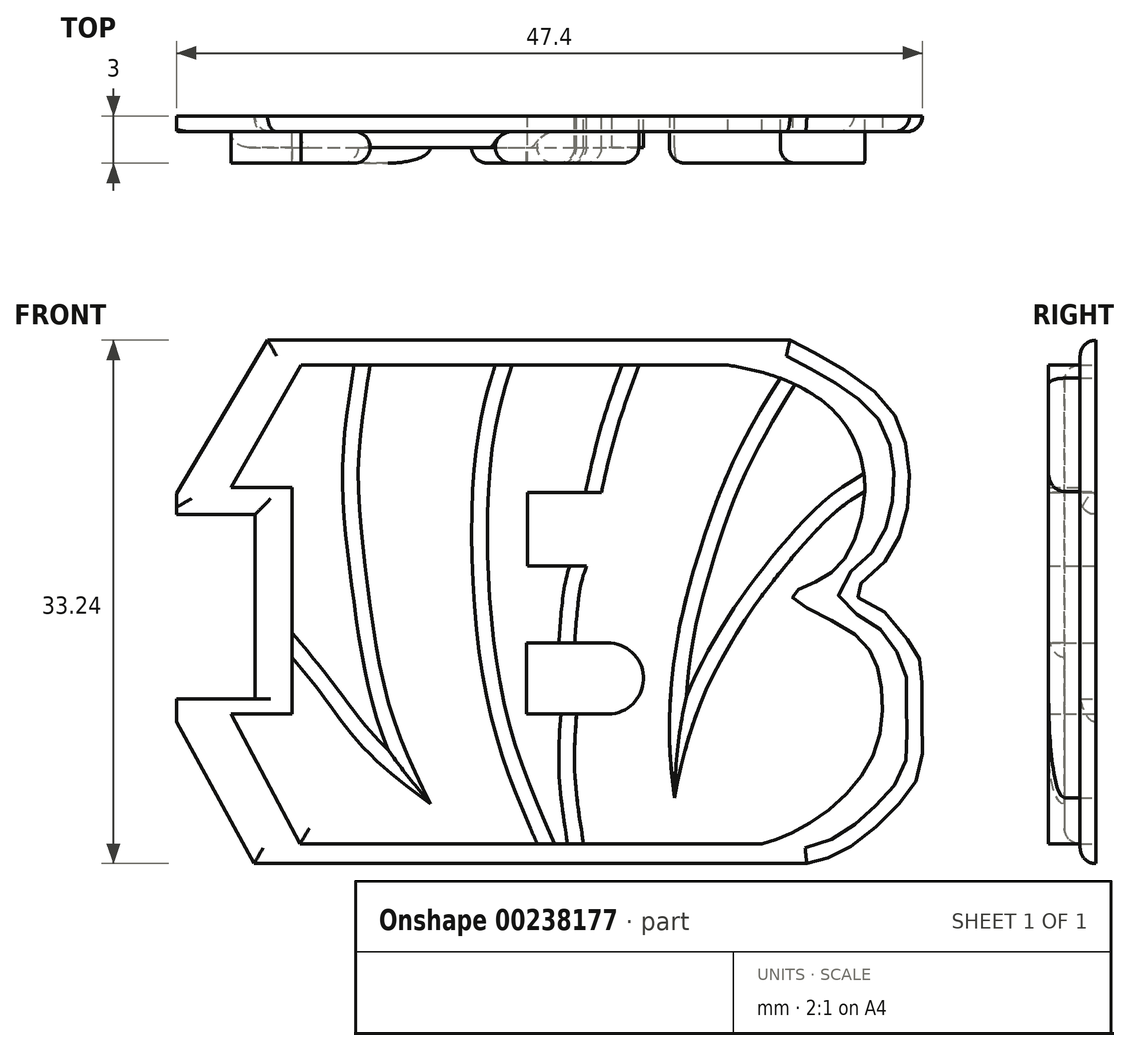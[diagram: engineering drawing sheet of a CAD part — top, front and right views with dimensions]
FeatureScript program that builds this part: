
annotation { "Feature Type Name" : "Feature", "Feature Type Description" : "" }
export const myFeature = defineFeature(function(context is Context, id is Id, definition is map)
    precondition{}
    {
        {
            var Q0;
            Q0=qCreatedBy(makeId("Front.planeOp"),FACE);
            var sketch = newSketch(context, id + "F0", { "sketchPlane" : qUnion([Q0])});
            skLineSegment(sketch, "E0", {"start": v(14.04, 53.13) * mm, "end": v(19.84, 62.86) * mm});
            skLineSegment(sketch, "E1", {"start": v(19.84, 62.86) * mm, "end": v(53.01, 62.86) * mm});
            skFitSpline(sketch, "E2", {"points": [v(53.01, 62.86) * mm, v(55.4, 61.6) * mm, v(58.74, 59.26) * mm, v(60.2, 56.87) * mm, v(60.6, 53.6) * mm, v(60.07, 50.67) * mm, v(58.67, 48.4) * mm, v(57.07, 46.8) * mm, v(58.67, 45.87) * mm, v(60.94, 43.14) * mm, v(61.34, 42.28) * mm, v(61.4, 38.95) * mm, v(61.27, 35.55) * mm, v(60, 33.48) * mm, v(57.6, 31.22) * mm, v(55.54, 30.02) * mm, v(54.08, 29.62) * mm], "startDerivative": vector(35.52, -17.88) * mm, "endDerivative": vector(-30.19, -6.38) * mm});
            skLineSegment(sketch, "E3", {"start": v(54.08, 29.62) * mm, "end": v(18.97, 29.62) * mm});
            skLineSegment(sketch, "E4", {"start": v(18.97, 29.62) * mm, "end": v(14.04, 38.61) * mm});
            skLineSegment(sketch, "E5", {"start": v(14.04, 38.61) * mm, "end": v(14.04, 40.08) * mm});
            skLineSegment(sketch, "E6", {"start": v(14.04, 40.08) * mm, "end": v(18.5, 40.08) * mm});
            skLineSegment(sketch, "E7", {"start": v(19.04, 40.74) * mm, "end": v(19.04, 51.8) * mm});
            skLineSegment(sketch, "E8", {"start": v(19.04, 51.8) * mm, "end": v(14.04, 51.8) * mm});
            skLineSegment(sketch, "E9", {"start": v(14.04, 51.8) * mm, "end": v(14.04, 53.13) * mm});
            skLineSegment(sketch, "E10", {"start": v(19.04, 40.74) * mm, "end": v(19.04, 40.07) * mm});
            skLineSegment(sketch, "E11", {"start": v(19.04, 40.07) * mm, "end": v(18.5, 40.08) * mm});
            skLineSegment(sketch, "E12", {"start": v(17.51, 53.52) * mm, "end": v(21.96, 61.29) * mm});
            skLineSegment(sketch, "E13", {"start": v(21.96, 61.29) * mm, "end": v(49.06, 61.29) * mm});
            skLineSegment(sketch, "E14", {"start": v(17.51, 53.52) * mm, "end": v(21.4, 53.52) * mm});
            skLineSegment(sketch, "E15", {"start": v(21.4, 53.52) * mm, "end": v(21.4, 39.13) * mm});
            skLineSegment(sketch, "E16", {"start": v(21.4, 39.13) * mm, "end": v(17.51, 39.13) * mm});
            skLineSegment(sketch, "E17", {"start": v(17.51, 39.13) * mm, "end": v(21.89, 30.87) * mm});
            skLineSegment(sketch, "E18", {"start": v(21.89, 30.87) * mm, "end": v(51.25, 30.87) * mm});
            skFitSpline(sketch, "E19", {"points": [v(51.25, 30.87) * mm, v(53.15, 31.58) * mm, v(56.47, 33.9) * mm, v(58.66, 37.57) * mm, v(58.66, 41.67) * mm, v(56.9, 44.35) * mm, v(53.15, 46.6) * mm, v(54.7, 47.53) * mm, v(56.75, 49.43) * mm, v(57.74, 54.09) * mm, v(55.77, 58.4) * mm, v(52.02, 60.58) * mm, v(49.06, 61.29) * mm], "startDerivative": vector(28.18, 8.53) * mm, "endDerivative": vector(-37.02, 6.74) * mm});
            skLineSegment(sketch, "E20", {"start": v(36.29, 39.13) * mm, "end": v(36.29, 43.64) * mm});
            skLineSegment(sketch, "E21", {"start": v(36.29, 43.64) * mm, "end": v(41.44, 43.64) * mm});
            skLineSegment(sketch, "E22", {"start": v(36.29, 39.13) * mm, "end": v(41.72, 39.13) * mm});
            skArc(sketch, "E23", {"start": v(41.44, 43.64) * mm, "mid": v(43.7, 41.52) * mm, "end": v(41.72, 39.13) * mm});
            skLineSegment(sketch, "E24", {"start": v(36.36, 48.51) * mm, "end": v(36.36, 53.2) * mm});
            skLineSegment(sketch, "E25", {"start": v(36.36, 53.2) * mm, "end": v(41.44, 53.2) * mm});
            skLineSegment(sketch, "E26", {"start": v(36.36, 48.51) * mm, "end": v(41.63, 48.51) * mm});
            skPoint(sketch, "E27.3.internal.snap0", {"position": v(38.9, 53.2) * mm});
            skFitSpline(sketch, "E28", {"points": [v(41.63, 48.51) * mm, v(42.75, 49.1) * mm, v(43.41, 50.24) * mm, v(43.32, 51.79) * mm, v(42.75, 52.72) * mm, v(41.44, 53.2) * mm], "startDerivative": vector(6.1, 2.42) * mm, "endDerivative": vector(-7.14, 1.68) * mm});
            skFitSpline(sketch, "E29", {"points": [v(34.3, 61.29) * mm, v(33.63, 58.94) * mm, v(32.92, 54.27) * mm, v(33.05, 45.07) * mm, v(34.56, 37.02) * mm, v(36.96, 30.87) * mm], "startDerivative": vector(-5.32, -17.12) * mm, "endDerivative": vector(12.35, -28.27) * mm});
            skFitSpline(sketch, "E30", {"points": [v(43.41, 61.29) * mm, v(42.03, 57.25) * mm, v(41.03, 53.2) * mm], "startDerivative": vector(-2.94, -8) * mm, "endDerivative": vector(-1.82, -8.19) * mm});
            skFitSpline(sketch, "E31", {"points": [v(40.1, 48.51) * mm, v(39.73, 47.34) * mm, v(39.34, 43.64) * mm], "startDerivative": vector(-1.1, -2.73) * mm, "endDerivative": vector(-0.49, -6.66) * mm});
            skFitSpline(sketch, "E32", {"points": [v(39.46, 39.13) * mm, v(39.34, 35.47) * mm, v(39.9, 30.87) * mm], "startDerivative": vector(-0.56, -7.56) * mm, "endDerivative": vector(1.41, -8.93) * mm});
            skFitSpline(sketch, "E33", {"points": [v(21.4, 42.7) * mm, v(23.37, 40.25) * mm, v(26.06, 36.84) * mm, v(30.18, 33.4) * mm], "startDerivative": vector(6.77, -8.11) * mm, "endDerivative": vector(11.74, -8.81) * mm});
            skFitSpline(sketch, "E34", {"points": [v(52.4, 60.45) * mm, v(51.25, 58.6) * mm, v(49.04, 54.31) * mm, v(47.3, 49.52) * mm, v(45.95, 44.37) * mm, v(45.35, 38.03) * mm, v(45.67, 33.8) * mm], "startDerivative": vector(-9.1, -14.25) * mm, "endDerivative": vector(2.9, -24.71) * mm});
            skFitSpline(sketch, "E35", {"points": [v(45.67, 33.8) * mm, v(46.12, 35.86) * mm, v(47.23, 39.55) * mm, v(49.2, 43.55) * mm, v(51.5, 47) * mm, v(55.66, 51.75) * mm, v(57.76, 53.25) * mm], "startDerivative": vector(3.17, 15.46) * mm, "endDerivative": vector(14, 8.38) * mm});
            skFitSpline(sketch, "E36", {"points": [v(30.18, 33.4) * mm, v(27.6, 39.53) * mm, v(26.18, 47.33) * mm, v(25.6, 54.63) * mm, v(26.35, 61.29) * mm], "startDerivative": vector(-11.9, 24.29) * mm, "endDerivative": vector(4.43, 27.26) * mm});
            skSolve(sketch);
        }
        {
            var Q0;
            Q0=makeQuery(id+"F0.imprint","IMPRINT",FACE,{"disambiguationData":[TD([[makeQuery(id+"F0.imprint","IMPRINT",EDGE,{"derivedFrom":sQuery(id+"F0.wireOp",EDGE,"E0")}),-1.0]])]});
            extrude(context, id + "F1", {"entities" : qUnion([Q0]), "depth" : 1 * mm});
        }
        {
            var Q0;
            {var subQ1=sQuery(id+"F0.wireOp",EDGE,"E16");Q0=makeQuery(id+"F0.imprint","IMPRINT",FACE,{"disambiguationData":[TD([[makeQuery(id+"F0.imprint","IMPRINT",EDGE,{"derivedFrom":subQ1}),1.0]])]});}
            var Q1;
            {var subQ5=sQuery(id+"F0.wireOp",EDGE,"E23");Q1=makeQuery(id+"F0.imprint","IMPRINT",FACE,{"disambiguationData":[TD([[makeQuery(id+"F0.imprint","IMPRINT",EDGE,{"derivedFrom":subQ5}),1.0]])]});}
            extrude(context, id + "F2", {"entities" : qUnion([Q0, Q1]), "operationType" : NewBodyOperationType.ADD, "depth" : 2 * mm});
        }
        {
            var Q0;
            {var subQ4=sQuery(id+"F0.wireOp",EDGE,"E12");Q0=makeQuery(id+"F0.imprint","IMPRINT",FACE,{"disambiguationData":[TD([[makeQuery(id+"F0.imprint","IMPRINT",EDGE,{"derivedFrom":subQ4}),-1.0]])]});}
            var Q1;
            {var subQ4=sQuery(id+"F0.wireOp",EDGE,"E20");Q1=makeQuery(id+"F0.imprint","IMPRINT",FACE,{"disambiguationData":[TD([[makeQuery(id+"F0.imprint","IMPRINT",EDGE,{"derivedFrom":subQ4}),1.0]])]});}
            var Q2;
            {var subQ0=sQuery(id+"F0.wireOp",EDGE,"E34");Q2=makeQuery(id+"F0.imprint","IMPRINT",FACE,{"disambiguationData":[TD([[makeQuery(id+"F0.imprint","IMPRINT",EDGE,{"derivedFrom":subQ0}),1.0]])]});}
            extrude(context, id + "F3", {"entities" : qUnion([Q0, Q1, Q2]), "operationType" : NewBodyOperationType.ADD, "depth" : 3 * mm});
        }
        {
            var Q0;
            Q0=makeQuery(id+"F3.opExtrude","CAP_EDGE",EDGE,{"disambiguationData":[OSD([sQuery(id+"F0.wireOp",EDGE,"E33")])],"isStart":false});
            var Q1;
            Q1=makeQuery(id+"F3.opExtrude","CAP_EDGE",EDGE,{"disambiguationData":[OSD([sQuery(id+"F0.wireOp",EDGE,"E36")])],"isStart":false});
            var Q2;
            Q2=makeQuery(id+"F3.opExtrude","CAP_EDGE",EDGE,{"disambiguationData":[OSD([sQuery(id+"F0.wireOp",EDGE,"E29")])],"isStart":false});
            var Q3;
            Q3=makeQuery(id+"F3.opExtrude","CAP_EDGE",EDGE,{"disambiguationData":[OSD([sQuery(id+"F0.wireOp",EDGE,"E32")])],"isStart":false});
            var Q4;
            Q4=makeQuery(id+"F3.opExtrude","CAP_EDGE",EDGE,{"disambiguationData":[OSD([sQuery(id+"F0.wireOp",EDGE,"E31")])],"isStart":false});
            var Q5;
            Q5=makeQuery(id+"F3.opExtrude","CAP_EDGE",EDGE,{"disambiguationData":[OSD([sQuery(id+"F0.wireOp",EDGE,"E30")])],"isStart":false});
            var Q6;
            Q6=makeQuery(id+"F3.opExtrude","CAP_EDGE",EDGE,{"disambiguationData":[OSD([sQuery(id+"F0.wireOp",EDGE,"E35")])],"isStart":false});
            var Q7;
            Q7=makeQuery(id+"F3.opExtrude","CAP_EDGE",EDGE,{"disambiguationData":[OSD([sQuery(id+"F0.wireOp",EDGE,"E34")])],"isStart":false});
            fillet(context, id + "F4", {"entities" : qUnion([Q0, Q1, Q2, Q3, Q4, Q5, Q6, Q7]), "radius" : 1 * mm, "tangentPropagation" : true, "allowEdgeOverflow" : false});
        }
        {
            var Q0;
            {var subQ0=sQuery(id+"F0.wireOp",EDGE,"E13");Q0=makeQuery(id+"F2.opExtrude","CAP_EDGE",EDGE,{"disambiguationData":[OSD([subQ0]),TDD([makeQuery(id+"F0.imprint","IMPRINT",EDGE,{"disambiguationData":[TD([[makeQuery(id+"F0.imprint","INTERSECT",VERTEX,{"derivedFrom":[subQ0,sQuery(id+"F0.wireOp",EDGE,"E29")]}),1.0]])],"derivedFrom":subQ0})])],"isStart":false});}
            var Q1;
            {var subQ0=sQuery(id+"F0.wireOp",EDGE,"E13");Q1=makeQuery(id+"F2.opExtrude","CAP_EDGE",EDGE,{"disambiguationData":[OSD([subQ0]),TDD([makeQuery(id+"F0.imprint","IMPRINT",EDGE,{"disambiguationData":[TD([[makeQuery(id+"F0.imprint","INTERSECT",VERTEX,{"derivedFrom":[subQ0,sQuery(id+"F0.wireOp",EDGE,"E19")]}),1.0]])],"derivedFrom":subQ0})])],"isStart":false});}
            var Q2;
            Q2=makeQuery(id+"F2.opExtrude","CAP_EDGE",EDGE,{"disambiguationData":[OSD([sQuery(id+"F0.wireOp",EDGE,"E17")])],"isStart":false});
            var Q3;
            {var subQ0=sQuery(id+"F0.wireOp",EDGE,"E18");Q3=makeQuery(id+"F2.opExtrude","CAP_EDGE",EDGE,{"disambiguationData":[OSD([subQ0]),TDD([makeQuery(id+"F0.imprint","IMPRINT",EDGE,{"disambiguationData":[TD([[makeQuery(id+"F0.imprint","INTERSECT",VERTEX,{"derivedFrom":[sQuery(id+"F0.wireOp",EDGE,"E17"),subQ0]}),-1.0]])],"derivedFrom":subQ0})])],"isStart":false});}
            var Q4;
            {var subQ0=sQuery(id+"F0.wireOp",EDGE,"E19");Q4=makeQuery(id+"F2.opExtrude","CAP_EDGE",EDGE,{"disambiguationData":[OSD([subQ0]),TDD([makeQuery(id+"F0.imprint","IMPRINT",EDGE,{"disambiguationData":[TD([[makeQuery(id+"F0.imprint","INTERSECT",VERTEX,{"derivedFrom":[sQuery(id+"F0.wireOp",EDGE,"E18"),subQ0]}),-1.0]])],"derivedFrom":subQ0})])],"isStart":false});}
            var Q5;
            {var subQ0=sQuery(id+"F0.wireOp",EDGE,"E18");Q5=makeQuery(id+"F2.opExtrude","CAP_EDGE",EDGE,{"disambiguationData":[OSD([subQ0]),TDD([makeQuery(id+"F0.imprint","IMPRINT",EDGE,{"disambiguationData":[TD([[makeQuery(id+"F0.imprint","INTERSECT",VERTEX,{"derivedFrom":[subQ0,sQuery(id+"F0.wireOp",EDGE,"E19")]}),1.0]])],"derivedFrom":subQ0})])],"isStart":false});}
            var Q6;
            Q6=makeQuery(id+"F1.opExtrude","CAP_EDGE",EDGE,{"disambiguationData":[OSD([sQuery(id+"F0.wireOp",EDGE,"E2")])],"isStart":false});
            var Q7;
            Q7=makeQuery(id+"F1.opExtrude","CAP_EDGE",EDGE,{"disambiguationData":[OSD([sQuery(id+"F0.wireOp",EDGE,"E3")])],"isStart":false});
            var Q8;
            Q8=makeQuery(id+"F1.opExtrude","CAP_EDGE",EDGE,{"disambiguationData":[OSD([sQuery(id+"F0.wireOp",EDGE,"E7"),sQuery(id+"F0.wireOp",EDGE,"E10")])],"isStart":false});
            var Q9;
            Q9=makeQuery(id+"F1.opExtrude","CAP_EDGE",EDGE,{"disambiguationData":[OSD([sQuery(id+"F0.wireOp",EDGE,"E8")])],"isStart":false});
            var Q10;
            Q10=makeQuery(id+"F1.opExtrude","CAP_EDGE",EDGE,{"disambiguationData":[OSD([sQuery(id+"F0.wireOp",EDGE,"E0")])],"isStart":false});
            var Q11;
            Q11=makeQuery(id+"F1.opExtrude","CAP_EDGE",EDGE,{"disambiguationData":[OSD([sQuery(id+"F0.wireOp",EDGE,"E4")])],"isStart":false});
            var Q12;
            Q12=makeQuery(id+"F1.opExtrude","CAP_EDGE",EDGE,{"disambiguationData":[OSD([sQuery(id+"F0.wireOp",EDGE,"E1")])],"isStart":false});
            fillet(context, id + "F5", {"entities" : qUnion([Q0, Q1, Q2, Q3, Q4, Q5, Q6, Q7, Q8, Q9, Q10, Q11, Q12]), "radius" : 1 * mm, "tangentPropagation" : true, "allowEdgeOverflow" : false});
        }
        {
            var Q0;
            Q0=makeQuery(id+"F2.opExtrude","CAP_FACE",FACE,{"disambiguationData":[OSD([sQuery(id+"F0.wireOp",EDGE,"E13"),sQuery(id+"F0.wireOp",EDGE,"E18"),sQuery(id+"F0.wireOp",EDGE,"E19"),sQuery(id+"F0.wireOp",EDGE,"E21"),sQuery(id+"F0.wireOp",EDGE,"E22"),sQuery(id+"F0.wireOp",EDGE,"E23"),sQuery(id+"F0.wireOp",EDGE,"E25"),sQuery(id+"F0.wireOp",EDGE,"E26"),sQuery(id+"F0.wireOp",EDGE,"E28"),sQuery(id+"F0.wireOp",EDGE,"E30"),sQuery(id+"F0.wireOp",EDGE,"E31"),sQuery(id+"F0.wireOp",EDGE,"E32"),sQuery(id+"F0.wireOp",EDGE,"E34"),sQuery(id+"F0.wireOp",EDGE,"E35")])],"isStart":false});
            var sketch = newSketch(context, id + "F6", { "sketchPlane" : qUnion([Q0])});
            skCircle(sketch, "E37", {"center": v(53.9, 35.79) * mm, "radius": 2 * mm});
            skSolve(sketch);
        }
        {
            var Q0;
            Q0=sQuery(id+"F6.wireOp",VERTEX,"E37.center");
            var Q1;
            Q1=makeQuery(id+"F1.opExtrude","SWEPT_BODY",BODY,{"disambiguationData":[OSD([sQuery(id+"F0.wireOp",EDGE,"E0"),sQuery(id+"F0.wireOp",EDGE,"E1"),sQuery(id+"F0.wireOp",EDGE,"E2"),sQuery(id+"F0.wireOp",EDGE,"E3"),sQuery(id+"F0.wireOp",EDGE,"E4"),sQuery(id+"F0.wireOp",EDGE,"E5"),sQuery(id+"F0.wireOp",EDGE,"E6"),sQuery(id+"F0.wireOp",EDGE,"E7"),sQuery(id+"F0.wireOp",EDGE,"E8"),sQuery(id+"F0.wireOp",EDGE,"E9"),sQuery(id+"F0.wireOp",EDGE,"E10"),sQuery(id+"F0.wireOp",EDGE,"E11"),sQuery(id+"F0.wireOp",EDGE,"E12"),sQuery(id+"F0.wireOp",EDGE,"E13"),sQuery(id+"F0.wireOp",EDGE,"E14"),sQuery(id+"F0.wireOp",EDGE,"E15"),sQuery(id+"F0.wireOp",EDGE,"E16"),sQuery(id+"F0.wireOp",EDGE,"E17"),sQuery(id+"F0.wireOp",EDGE,"E18"),sQuery(id+"F0.wireOp",EDGE,"E19")])]});
            hole(context, id + "F7", {"style" : HoleStyle.SIMPLE, "endStyle" : HoleEndStyle.THROUGH, "holeDiameter" : 4 * mm, "isTappedThrough" : true, "tappedDepth" : 12 * mm, "tapClearance" : 3, "locations" : qUnion([Q0]), "scope" : qUnion([Q1])});
        }
    });
